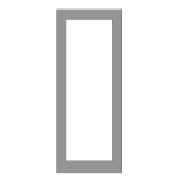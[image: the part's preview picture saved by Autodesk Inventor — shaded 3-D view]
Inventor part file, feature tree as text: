
AUTODESK INVENTOR PART (.ipt)
format: ipt  version: 2020 (Build 240168000, 168)  size: 190,464 bytes
history: native  units: in
note: dims shown in document units (in); Inventor stores cm internally (conversion verified against a paired STEP export)
features: sketch x5, other x4, plane x3, split x2, extrude x1, hole x1
ambient origin geometry x8: Origin, YZ Plane, XZ Plane, XY Plane, X Axis, Y Axis, Z Axis, Center Point
bodies: Solid1 (feature_tree), Body (feature_tree)
feature tree (16):
  other  "Driven Length"
  other  "Frame Generator"
  other  "Start Plane"
  other  "End Plane"
  plane  "Work Plane6"
  split  "Split1"
  plane  "Work Plane7"
  split  "Split2"
  extrude  "Extrusion3"  Depth=3.0in
  hole  "Hole1"  [1 undecoded]
  sketch  "Sketch"  dims[d8=0.13in d9=0.0in d14=90.0deg d11=30.0in d19=1.0in d20=0.0in d23=1.125in d26=0.5in d27=0.5in d28=0.7874in d30=28.0in d31=0.7874in d33=2.0in d36=0.196in d37=0.146in d38=0.385in d39=0.02in d40=0.5635in d41=1.0in d42=0.8108in d43=0.3135in d44=3.5in d45=0.3135in d46=3.5in d48=1.25in d49=2.0in d50=2.0in d51=1.25in d52=1.125in]
  sketch  "Sketch6"  dims[d0=1.0in d1=3.0in]
  plane  "Work Plane5"
  sketch  "Sketch7"  dims[d2=0.125in d3=0.125in]
  sketch  "Sketch8"  dims[d6=-0.5in]
  sketch  "Sketch9"  dims[d7=29.5in]
note: 1 required parameter value undecoded (feature->parameter linkage not recoverable at this tier; creation-order binding heuristic only, values carry confidence <= 0.55)
